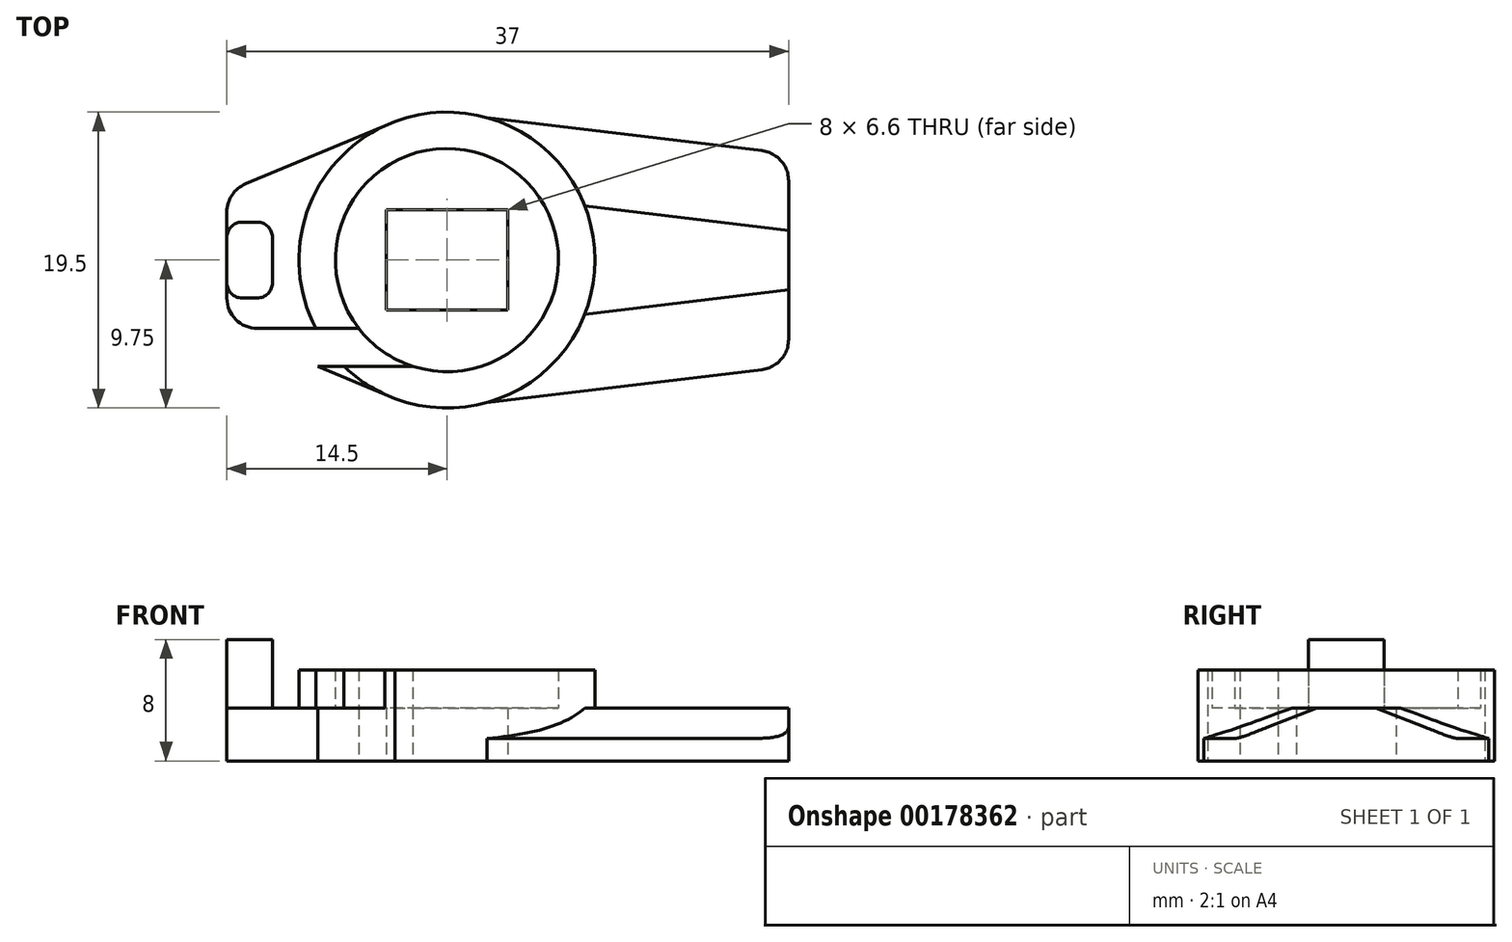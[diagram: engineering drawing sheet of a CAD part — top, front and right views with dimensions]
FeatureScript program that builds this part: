
annotation { "Feature Type Name" : "Feature", "Feature Type Description" : "" }
export const myFeature = defineFeature(function(context is Context, id is Id, definition is map)
    precondition{}
    {
        {
            var Q0;
            Q0=qCreatedBy(makeId("Top.planeOp"),FACE);
            var sketch = newSketch(context, id + "F0", { "sketchPlane" : qUnion([Q0])});
            skCircle(sketch, "E0", {"center": v(0, 0) * mm, "radius": 9.75 * mm});
            skLineSegment(sketch, "E1.bottom", {"start": v(14.5, -4.5) * mm, "end": v(-14.5, -4.5) * mm});
            skLineSegment(sketch, "E1.top", {"start": v(14.5, 4.5) * mm, "end": v(-14.5, 4.5) * mm});
            skLineSegment(sketch, "E1.left", {"start": v(14.5, -4.5) * mm, "end": v(14.5, 4.5) * mm});
            skLineSegment(sketch, "E1.right", {"start": v(-14.5, -4.5) * mm, "end": v(-14.5, 4.5) * mm});
            skLineSegment(sketch, "E2.bottom", {"start": v(22.5, -7) * mm, "end": v(-22.5, -7) * mm});
            skLineSegment(sketch, "E2.top", {"start": v(22.5, 7) * mm, "end": v(-22.5, 7) * mm});
            skLineSegment(sketch, "E2.left", {"start": v(22.5, -7) * mm, "end": v(22.5, 7) * mm});
            skLineSegment(sketch, "E2.right", {"start": v(-22.5, -7) * mm, "end": v(-22.5, 7) * mm});
            skLineSegment(sketch, "E3", {"start": v(-14.5, 4.5) * mm, "end": v(-3.43, 9.13) * mm});
            skLineSegment(sketch, "E4", {"start": v(-14.5, -4.5) * mm, "end": v(-3.43, -9.13) * mm});
            skLineSegment(sketch, "E5", {"start": v(22.5, 7) * mm, "end": v(2.64, 9.39) * mm});
            skLineSegment(sketch, "E6", {"start": v(22.5, -7) * mm, "end": v(2.64, -9.39) * mm});
            skCircle(sketch, "E7", {"center": v(0, 0) * mm, "radius": 7.35 * mm});
            skLineSegment(sketch, "E8.bottom", {"start": v(4, -3.3) * mm, "end": v(-4, -3.3) * mm});
            skLineSegment(sketch, "E8.top", {"start": v(4, 3.3) * mm, "end": v(-4, 3.3) * mm});
            skLineSegment(sketch, "E8.left", {"start": v(4, -3.3) * mm, "end": v(4, 3.3) * mm});
            skLineSegment(sketch, "E8.right", {"start": v(-4, -3.3) * mm, "end": v(-4, 3.3) * mm});
            skLineSegment(sketch, "E9.bottom", {"start": v(-14.5, -2.5) * mm, "end": v(-11.5, -2.5) * mm});
            skLineSegment(sketch, "E9.top", {"start": v(-14.5, 2.5) * mm, "end": v(-11.5, 2.5) * mm});
            skLineSegment(sketch, "E9.left", {"start": v(-14.5, -2.5) * mm, "end": v(-14.5, 2.5) * mm});
            skLineSegment(sketch, "E9.right", {"start": v(-11.5, -2.5) * mm, "end": v(-11.5, 2.5) * mm});
            skPoint(sketch, "E9.middle", {"position": v(-13, 0) * mm});
            skSolve(sketch);
        }
        {
            var Q0;
            {var subQ4=sQuery(id+"F0.wireOp",EDGE,"E9.bottom");Q0=makeQuery(id+"F0.imprint","IMPRINT",FACE,{"disambiguationData":[TD([[makeQuery(id+"F0.imprint","IMPRINT",EDGE,{"derivedFrom":subQ4}),-1.0]])]});}
            var Q1;
            {var subQ0=sQuery(id+"F0.wireOp",EDGE,"E2.top");var subQ1=sQuery(id+"F0.wireOp",EDGE,"E0");var subQ2=makeQuery(id+"F0.imprint","INTERSECT",VERTEX,{"disambiguationData":[OD(1.0)],"derivedFrom":[subQ1,subQ0]});Q1=makeQuery(id+"F0.imprint","IMPRINT",FACE,{"disambiguationData":[TD([[makeQuery(id+"F0.imprint","IMPRINT",EDGE,{"disambiguationData":[TD([[subQ2,-1.0]])],"derivedFrom":subQ1}),-1.0]])]});}
            var Q2;
            {var subQ0=sQuery(id+"F0.wireOp",EDGE,"E3");var subQ1=sQuery(id+"F0.wireOp",EDGE,"E0");var subQ2=makeQuery(id+"F0.imprint","INTERSECT",VERTEX,{"disambiguationData":[OD(1.0)],"derivedFrom":[subQ1,subQ0]});Q2=makeQuery(id+"F0.imprint","IMPRINT",FACE,{"disambiguationData":[TD([[makeQuery(id+"F0.imprint","IMPRINT",EDGE,{"disambiguationData":[TD([[subQ2,-1.0]])],"derivedFrom":subQ1}),-1.0]])]});}
            var Q3;
            {var subQ0=sQuery(id+"F0.wireOp",EDGE,"E5");Q3=makeQuery(id+"F0.imprint","IMPRINT",FACE,{"disambiguationData":[TD([[makeQuery(id+"F0.imprint","IMPRINT",EDGE,{"derivedFrom":subQ0}),1.0]])]});}
            var Q4;
            {var subQ0=sQuery(id+"F0.wireOp",EDGE,"E2.top");var subQ1=sQuery(id+"F0.wireOp",EDGE,"E0");var subQ2=makeQuery(id+"F0.imprint","INTERSECT",VERTEX,{"disambiguationData":[OD(0.0)],"derivedFrom":[subQ1,subQ0]});Q4=makeQuery(id+"F0.imprint","IMPRINT",FACE,{"disambiguationData":[TD([[makeQuery(id+"F0.imprint","IMPRINT",EDGE,{"disambiguationData":[TD([[subQ2,1.0]])],"derivedFrom":subQ1}),-1.0]])]});}
            var Q5;
            {var subQ0=sQuery(id+"F0.wireOp",EDGE,"E1.top");var subQ1=sQuery(id+"F0.wireOp",EDGE,"E0");var subQ2=makeQuery(id+"F0.imprint","INTERSECT",VERTEX,{"disambiguationData":[OD(0.0)],"derivedFrom":[subQ1,subQ0]});Q5=makeQuery(id+"F0.imprint","IMPRINT",FACE,{"disambiguationData":[TD([[makeQuery(id+"F0.imprint","IMPRINT",EDGE,{"disambiguationData":[TD([[subQ2,1.0]])],"derivedFrom":subQ1}),-1.0]])]});}
            var Q6;
            {var subQ0=sQuery(id+"F0.wireOp",EDGE,"E2.bottom");var subQ1=sQuery(id+"F0.wireOp",EDGE,"E0");var subQ2=makeQuery(id+"F0.imprint","INTERSECT",VERTEX,{"disambiguationData":[OD(1.0)],"derivedFrom":[subQ1,subQ0]});Q6=makeQuery(id+"F0.imprint","IMPRINT",FACE,{"disambiguationData":[TD([[makeQuery(id+"F0.imprint","IMPRINT",EDGE,{"disambiguationData":[TD([[subQ2,-1.0]])],"derivedFrom":subQ1}),-1.0]])]});}
            var Q7;
            {var subQ0=sQuery(id+"F0.wireOp",EDGE,"E6");Q7=makeQuery(id+"F0.imprint","IMPRINT",FACE,{"disambiguationData":[TD([[makeQuery(id+"F0.imprint","IMPRINT",EDGE,{"derivedFrom":subQ0}),-1.0]])]});}
            var Q8;
            {var subQ0=sQuery(id+"F0.wireOp",EDGE,"E4");var subQ1=sQuery(id+"F0.wireOp",EDGE,"E0");var subQ2=makeQuery(id+"F0.imprint","INTERSECT",VERTEX,{"disambiguationData":[OD(1.0)],"derivedFrom":[subQ1,subQ0]});Q8=makeQuery(id+"F0.imprint","IMPRINT",FACE,{"disambiguationData":[TD([[makeQuery(id+"F0.imprint","IMPRINT",EDGE,{"disambiguationData":[TD([[subQ2,1.0]])],"derivedFrom":subQ1}),-1.0]])]});}
            var Q9;
            {var subQ0=sQuery(id+"F0.wireOp",EDGE,"E1.bottom");var subQ1=sQuery(id+"F0.wireOp",EDGE,"E0");var subQ2=makeQuery(id+"F0.imprint","INTERSECT",VERTEX,{"disambiguationData":[OD(0.0)],"derivedFrom":[subQ1,subQ0]});Q9=makeQuery(id+"F0.imprint","IMPRINT",FACE,{"disambiguationData":[TD([[makeQuery(id+"F0.imprint","IMPRINT",EDGE,{"disambiguationData":[TD([[subQ2,-1.0]])],"derivedFrom":subQ1}),-1.0]])]});}
            var Q10;
            {var subQ0=sQuery(id+"F0.wireOp",EDGE,"E7");var subQ1=sQuery(id+"F0.wireOp",EDGE,"E1.bottom");var subQ2=makeQuery(id+"F0.imprint","INTERSECT",VERTEX,{"disambiguationData":[OD(0.0)],"derivedFrom":[subQ1,subQ0]});Q10=makeQuery(id+"F0.imprint","IMPRINT",FACE,{"disambiguationData":[TD([[makeQuery(id+"F0.imprint","IMPRINT",EDGE,{"disambiguationData":[TD([[subQ2,-1.0]])],"derivedFrom":subQ1}),1.0]])]});}
            var Q11;
            {var subQ0=sQuery(id+"F0.wireOp",EDGE,"E7");var subQ1=sQuery(id+"F0.wireOp",EDGE,"E2.bottom");var subQ2=makeQuery(id+"F0.imprint","INTERSECT",VERTEX,{"disambiguationData":[OD(0.0)],"derivedFrom":[subQ1,subQ0]});Q11=makeQuery(id+"F0.imprint","IMPRINT",FACE,{"disambiguationData":[TD([[makeQuery(id+"F0.imprint","IMPRINT",EDGE,{"disambiguationData":[TD([[subQ2,-1.0]])],"derivedFrom":subQ1}),1.0]])]});}
            var Q12;
            Q12=makeQuery(id+"F0.imprint","IMPRINT",FACE,{"disambiguationData":[TD([[makeQuery(id+"F0.imprint","IMPRINT",EDGE,{"derivedFrom":sQuery(id+"F0.wireOp",EDGE,"E8.bottom")}),1.0]])]});
            var Q13;
            {var subQ0=sQuery(id+"F0.wireOp",EDGE,"E7");var subQ1=sQuery(id+"F0.wireOp",EDGE,"E1.top");var subQ2=makeQuery(id+"F0.imprint","INTERSECT",VERTEX,{"disambiguationData":[OD(0.0)],"derivedFrom":[subQ1,subQ0]});Q13=makeQuery(id+"F0.imprint","IMPRINT",FACE,{"disambiguationData":[TD([[makeQuery(id+"F0.imprint","IMPRINT",EDGE,{"disambiguationData":[TD([[subQ2,-1.0]])],"derivedFrom":subQ1}),-1.0]])]});}
            var Q14;
            {var subQ0=sQuery(id+"F0.wireOp",EDGE,"E7");var subQ1=sQuery(id+"F0.wireOp",EDGE,"E2.top");var subQ2=makeQuery(id+"F0.imprint","INTERSECT",VERTEX,{"disambiguationData":[OD(0.0)],"derivedFrom":[subQ1,subQ0]});Q14=makeQuery(id+"F0.imprint","IMPRINT",FACE,{"disambiguationData":[TD([[makeQuery(id+"F0.imprint","IMPRINT",EDGE,{"disambiguationData":[TD([[subQ2,-1.0]])],"derivedFrom":subQ1}),-1.0]])]});}
            extrude(context, id + "F1", {"entities" : qUnion([Q0, Q1, Q2, Q3, Q4, Q5, Q6, Q7, Q8, Q9, Q10, Q11, Q12, Q13, Q14]), "depth" : 3.5 * mm});
        }
        {
            var Q0;
            Q0=makeQuery(id+"F0.imprint","IMPRINT",FACE,{"disambiguationData":[TD([[makeQuery(id+"F0.imprint","IMPRINT",EDGE,{"derivedFrom":sQuery(id+"F0.wireOp",EDGE,"E9.bottom")}),1.0]])]});
            extrude(context, id + "F2", {"entities" : qUnion([Q0]), "operationType" : NewBodyOperationType.ADD, "depth" : 8 * mm});
        }
        {
            var Q0;
            {var subQ0=sQuery(id+"F0.wireOp",EDGE,"E1.top");var subQ1=sQuery(id+"F0.wireOp",EDGE,"E0");var subQ2=makeQuery(id+"F0.imprint","INTERSECT",VERTEX,{"disambiguationData":[OD(1.0)],"derivedFrom":[subQ1,subQ0]});Q0=makeQuery(id+"F0.imprint","IMPRINT",FACE,{"disambiguationData":[TD([[makeQuery(id+"F0.imprint","IMPRINT",EDGE,{"disambiguationData":[TD([[subQ2,-1.0]])],"derivedFrom":subQ1}),1.0]])]});}
            var Q1;
            {var subQ0=sQuery(id+"F0.wireOp",EDGE,"E2.top");var subQ1=sQuery(id+"F0.wireOp",EDGE,"E0");var subQ2=makeQuery(id+"F0.imprint","INTERSECT",VERTEX,{"disambiguationData":[OD(1.0)],"derivedFrom":[subQ1,subQ0]});Q1=makeQuery(id+"F0.imprint","IMPRINT",FACE,{"disambiguationData":[TD([[makeQuery(id+"F0.imprint","IMPRINT",EDGE,{"disambiguationData":[TD([[subQ2,-1.0]])],"derivedFrom":subQ1}),1.0]])]});}
            var Q2;
            {var subQ1=sQuery(id+"F0.wireOp",EDGE,"E0");var subQ9=makeQuery(id+"F0.imprint","INTERSECT",VERTEX,{"derivedFrom":[subQ1,sQuery(id+"F0.wireOp",EDGE,"E5")]});Q2=makeQuery(id+"F0.imprint","IMPRINT",FACE,{"disambiguationData":[TD([[makeQuery(id+"F0.imprint","IMPRINT",EDGE,{"disambiguationData":[TD([[subQ9,1.0]])],"derivedFrom":subQ1}),1.0]])]});}
            var Q3;
            {var subQ0=sQuery(id+"F0.wireOp",EDGE,"E2.top");var subQ1=sQuery(id+"F0.wireOp",EDGE,"E0");var subQ2=makeQuery(id+"F0.imprint","INTERSECT",VERTEX,{"disambiguationData":[OD(0.0)],"derivedFrom":[subQ1,subQ0]});Q3=makeQuery(id+"F0.imprint","IMPRINT",FACE,{"disambiguationData":[TD([[makeQuery(id+"F0.imprint","IMPRINT",EDGE,{"disambiguationData":[TD([[subQ2,1.0]])],"derivedFrom":subQ1}),1.0]])]});}
            var Q4;
            {var subQ0=sQuery(id+"F0.wireOp",EDGE,"E1.top");var subQ1=sQuery(id+"F0.wireOp",EDGE,"E0");var subQ2=makeQuery(id+"F0.imprint","INTERSECT",VERTEX,{"disambiguationData":[OD(0.0)],"derivedFrom":[subQ1,subQ0]});Q4=makeQuery(id+"F0.imprint","IMPRINT",FACE,{"disambiguationData":[TD([[makeQuery(id+"F0.imprint","IMPRINT",EDGE,{"disambiguationData":[TD([[subQ2,1.0]])],"derivedFrom":subQ1}),1.0]])]});}
            var Q5;
            {var subQ0=sQuery(id+"F0.wireOp",EDGE,"E2.bottom");var subQ1=sQuery(id+"F0.wireOp",EDGE,"E0");var subQ2=makeQuery(id+"F0.imprint","INTERSECT",VERTEX,{"disambiguationData":[OD(1.0)],"derivedFrom":[subQ1,subQ0]});Q5=makeQuery(id+"F0.imprint","IMPRINT",FACE,{"disambiguationData":[TD([[makeQuery(id+"F0.imprint","IMPRINT",EDGE,{"disambiguationData":[TD([[subQ2,-1.0]])],"derivedFrom":subQ1}),1.0]])]});}
            var Q6;
            {var subQ1=sQuery(id+"F0.wireOp",EDGE,"E0");var subQ7=sQuery(id+"F0.wireOp",EDGE,"E4");var subQ9=makeQuery(id+"F0.imprint","INTERSECT",VERTEX,{"disambiguationData":[OD(1.0)],"derivedFrom":[subQ1,subQ7]});Q6=makeQuery(id+"F0.imprint","IMPRINT",FACE,{"disambiguationData":[TD([[makeQuery(id+"F0.imprint","IMPRINT",EDGE,{"disambiguationData":[TD([[subQ9,1.0]])],"derivedFrom":subQ1}),1.0]])]});}
            var Q7;
            {var subQ0=sQuery(id+"F0.wireOp",EDGE,"E1.bottom");var subQ1=sQuery(id+"F0.wireOp",EDGE,"E0");var subQ2=makeQuery(id+"F0.imprint","INTERSECT",VERTEX,{"disambiguationData":[OD(0.0)],"derivedFrom":[subQ1,subQ0]});Q7=makeQuery(id+"F0.imprint","IMPRINT",FACE,{"disambiguationData":[TD([[makeQuery(id+"F0.imprint","IMPRINT",EDGE,{"disambiguationData":[TD([[subQ2,-1.0]])],"derivedFrom":subQ1}),1.0]])]});}
            extrude(context, id + "F3", {"entities" : qUnion([Q0, Q1, Q2, Q3, Q4, Q5, Q6, Q7]), "operationType" : NewBodyOperationType.ADD, "depth" : 6 * mm});
        }
        {
            var Q0;
            Q0=makeQuery(id+"F1.opExtrude","CAP_EDGE",EDGE,{"disambiguationData":[OSD([sQuery(id+"F0.wireOp",EDGE,"E6")])],"isStart":false});
            var Q1;
            Q1=makeQuery(id+"F1.opExtrude","CAP_EDGE",EDGE,{"disambiguationData":[OSD([sQuery(id+"F0.wireOp",EDGE,"E5")])],"isStart":false});
            chamfer(context, id + "F4", {"entities" : qUnion([Q0, Q1]), "chamferType" : ChamferType.TWO_OFFSETS, "width1" : 2 * mm, "oppositeDirection" : false, "width2" : 5 * mm, "tangentPropagation" : true});
        }
        {
            var Q0;
            Q0=makeQuery(id+"F1.opExtrude","SWEPT_EDGE",EDGE,{"disambiguationData":[OSD([sQuery(id+"F0.wireOp",EDGE,"E1.bottom"),sQuery(id+"F0.wireOp",EDGE,"E1.right"),sQuery(id+"F0.wireOp",EDGE,"E4")])]});
            var Q1;
            Q1=makeQuery(id+"F1.opExtrude","SWEPT_EDGE",EDGE,{"disambiguationData":[OSD([sQuery(id+"F0.wireOp",EDGE,"E1.top"),sQuery(id+"F0.wireOp",EDGE,"E1.right"),sQuery(id+"F0.wireOp",EDGE,"E3")])]});
            var Q2;
            Q2=makeQuery(id+"F1.opExtrude","SWEPT_EDGE",EDGE,{"disambiguationData":[OSD([sQuery(id+"F0.wireOp",EDGE,"E2.bottom"),sQuery(id+"F0.wireOp",EDGE,"E2.left"),sQuery(id+"F0.wireOp",EDGE,"E6")])]});
            var Q3;
            Q3=makeQuery(id+"F1.opExtrude","SWEPT_EDGE",EDGE,{"disambiguationData":[OSD([sQuery(id+"F0.wireOp",EDGE,"E2.top"),sQuery(id+"F0.wireOp",EDGE,"E2.left"),sQuery(id+"F0.wireOp",EDGE,"E5")])]});
            fillet(context, id + "F5", {"entities" : qUnion([Q0, Q1, Q2, Q3]), "radius" : 2 * mm, "tangentPropagation" : true, "allowEdgeOverflow" : false});
        }
        {
            var Q0;
            Q0=makeQuery(id+"F2.opExtrude","SWEPT_EDGE",EDGE,{"disambiguationData":[OSD([sQuery(id+"F0.wireOp",EDGE,"E1.right"),sQuery(id+"F0.wireOp",EDGE,"E9.bottom"),sQuery(id+"F0.wireOp",EDGE,"E9.left")])]});
            var Q1;
            Q1=makeQuery(id+"F2.opExtrude","SWEPT_EDGE",EDGE,{"disambiguationData":[OSD([sQuery(id+"F0.wireOp",EDGE,"E9.bottom"),sQuery(id+"F0.wireOp",EDGE,"E9.right")])]});
            var Q2;
            Q2=makeQuery(id+"F2.opExtrude","SWEPT_EDGE",EDGE,{"disambiguationData":[OSD([sQuery(id+"F0.wireOp",EDGE,"E1.right"),sQuery(id+"F0.wireOp",EDGE,"E9.top"),sQuery(id+"F0.wireOp",EDGE,"E9.left")])]});
            var Q3;
            Q3=makeQuery(id+"F2.opExtrude","SWEPT_EDGE",EDGE,{"disambiguationData":[OSD([sQuery(id+"F0.wireOp",EDGE,"E9.top"),sQuery(id+"F0.wireOp",EDGE,"E9.right")])]});
            fillet(context, id + "F6", {"entities" : qUnion([Q0, Q1, Q2, Q3]), "radius" : 1 * mm, "tangentPropagation" : true, "allowEdgeOverflow" : false});
        }
    });
